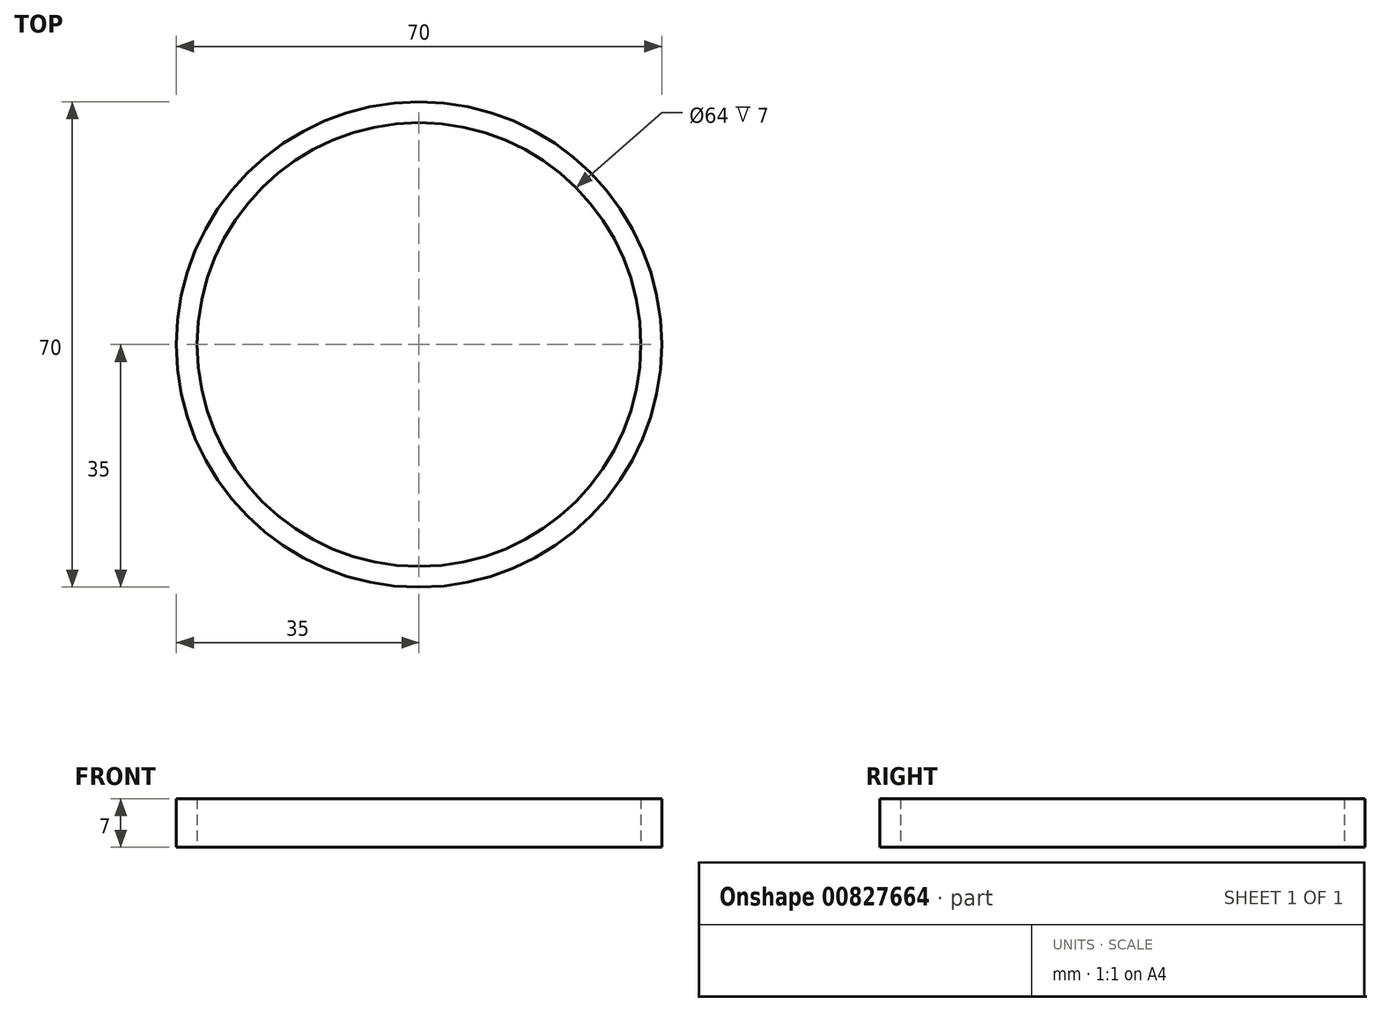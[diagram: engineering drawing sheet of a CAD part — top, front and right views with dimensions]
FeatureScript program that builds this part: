
annotation { "Feature Type Name" : "Feature", "Feature Type Description" : "" }
export const myFeature = defineFeature(function(context is Context, id is Id, definition is map)
    precondition{}
    {
        {
            var Q0;
            Q0=qCreatedBy(makeId("Top.planeOp"),FACE);
            var sketch = newSketch(context, id + "F0", { "sketchPlane" : qUnion([Q0])});
            skCircle(sketch, "E0", {"center": v(0, 0) * mm, "radius": 35 * mm});
            skCircle(sketch, "E1", {"center": v(0, 0) * mm, "radius": 32 * mm});
            skSolve(sketch);
        }
        {
            var Q0;
            Q0=makeQuery(id+"F0.imprint","IMPRINT",FACE,{"disambiguationData":[TD([[makeQuery(id+"F0.imprint","IMPRINT",EDGE,{"derivedFrom":sQuery(id+"F0.wireOp",EDGE,"E0")}),1.0]])]});
            extrude(context, id + "F1", {"entities" : qUnion([Q0]), "depth" : 7 * mm, "offsetDistance" : 25 * mm});
        }
    });
